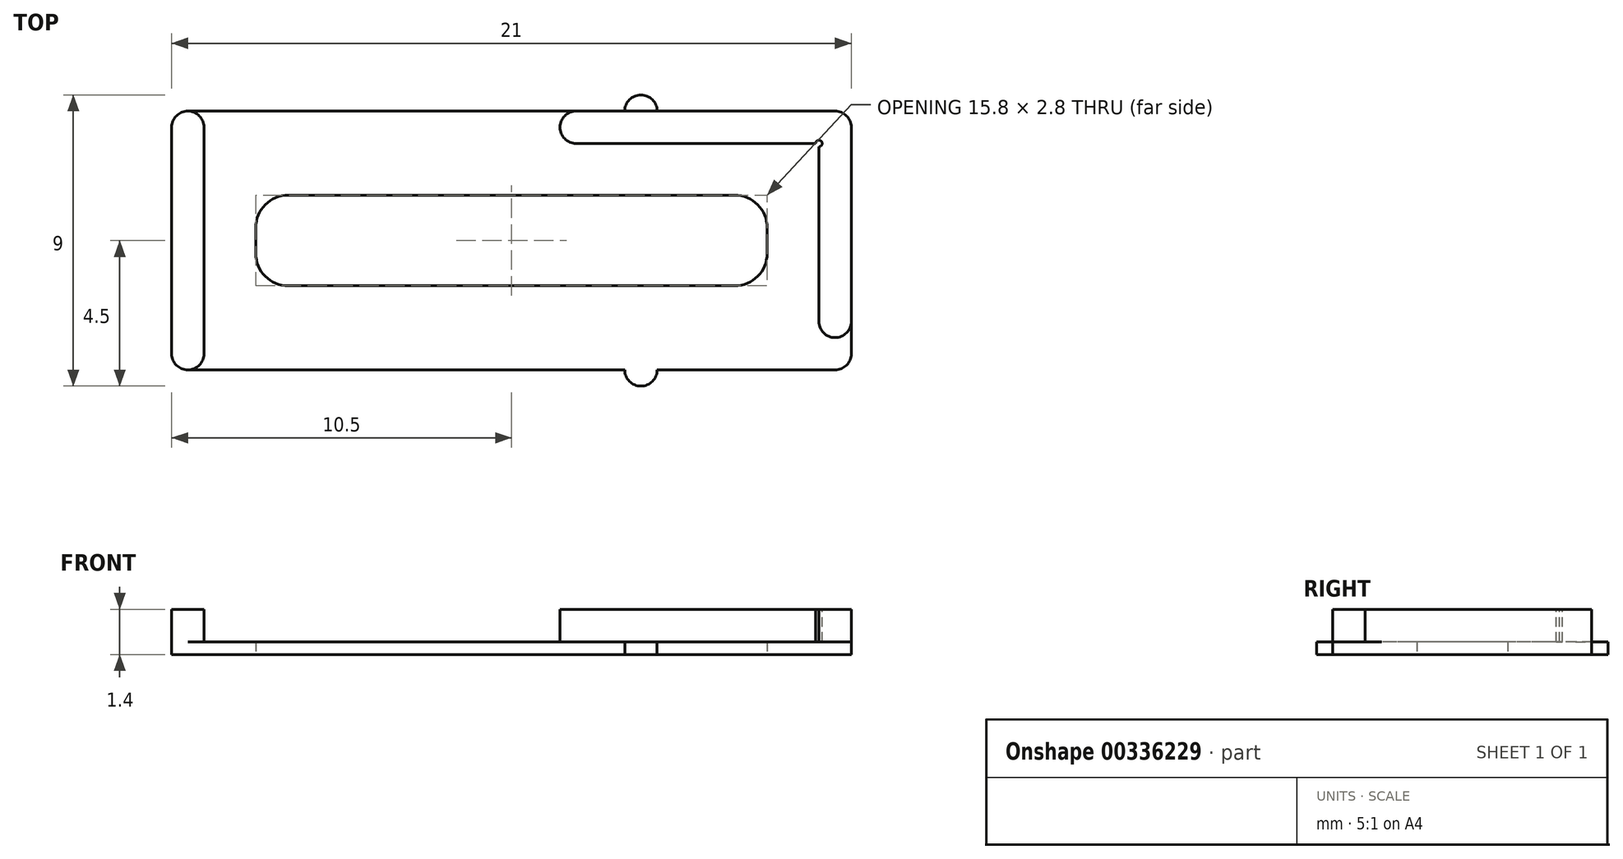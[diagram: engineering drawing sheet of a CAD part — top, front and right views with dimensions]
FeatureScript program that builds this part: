
annotation { "Feature Type Name" : "Feature", "Feature Type Description" : "" }
export const myFeature = defineFeature(function(context is Context, id is Id, definition is map)
    precondition{}
    {
        {
            var Q0;
            Q0=qCreatedBy(makeId("Top.planeOp"),FACE);
            var sketch = newSketch(context, id + "F0", { "sketchPlane" : qUnion([Q0])});
            skLineSegment(sketch, "E0.bottom", {"start": v(-4.5, 4.8) * mm, "end": v(4.5, 4.8) * mm});
            skLineSegment(sketch, "E0.top", {"start": v(-4.5, 0) * mm, "end": v(4.5, 0) * mm});
            skLineSegment(sketch, "E0.left", {"start": v(-4.5, 4.8) * mm, "end": v(-4.5, 0) * mm});
            skLineSegment(sketch, "E0.right", {"start": v(4.5, 4.8) * mm, "end": v(4.5, 0) * mm});
            skLineSegment(sketch, "E1", {"start": v(-4.5, 0) * mm, "end": v(-9.5, 0) * mm});
            skLineSegment(sketch, "E2", {"start": v(-9.5, 0) * mm, "end": v(-9.5, -6) * mm});
            skLineSegment(sketch, "E3", {"start": v(4.5, 0) * mm, "end": v(9.5, 0) * mm});
            skLineSegment(sketch, "E4", {"start": v(9.5, 0) * mm, "end": v(9.5, -6) * mm});
            skLineSegment(sketch, "E5", {"start": v(9.5, -6) * mm, "end": v(-9.5, -6) * mm});
            skLineSegment(sketch, "E6", {"start": v(-9.5, -1) * mm, "end": v(9.5, -1) * mm, "construction": true});
            skLineSegment(sketch, "E7", {"start": v(-9.5, -5.2) * mm, "end": v(9.5, -5.2) * mm, "construction": true});
            skPoint(sketch, "E8", {"position": v(4, -6) * mm});
            skPoint(sketch, "E9", {"position": v(4, 0) * mm});
            skSolve(sketch);
        }
        {
            var Q0;
            Q0=qCreatedBy(makeId("Front.planeOp"),FACE);
            var sketch = newSketch(context, id + "F1", { "sketchPlane" : qUnion([Q0])});
            skLineSegment(sketch, "E10", {"start": v(0, 0) * mm, "end": v(0, -0.4) * mm});
            skLineSegment(sketch, "E11", {"start": v(0, 0) * mm, "end": v(0, 1) * mm});
            skSolve(sketch);
        }
        {
            var Q0;
            Q0=qCreatedBy(makeId("Top.planeOp"),FACE);
            var sketch = newSketch(context, id + "F2", { "sketchPlane" : qUnion([Q0])});
            skLineSegment(sketch, "E12.0.0", {"start": v(4.5, 0) * mm, "end": v(-4.5, 0) * mm, "construction": true});
            skLineSegment(sketch, "E12.0.1", {"start": v(-4.5, 0) * mm, "end": v(-9.5, 0) * mm, "construction": true});
            skLineSegment(sketch, "E12.0.2", {"start": v(-9.5, 0) * mm, "end": v(-9.5, -6) * mm, "construction": true});
            skLineSegment(sketch, "E12.0.3", {"start": v(-9.5, -6) * mm, "end": v(9.5, -6) * mm, "construction": true});
            skLineSegment(sketch, "E12.0.4", {"start": v(9.5, -6) * mm, "end": v(9.5, 0) * mm, "construction": true});
            skLineSegment(sketch, "E12.0.5", {"start": v(9.5, 0) * mm, "end": v(4.5, 0) * mm, "construction": true});
            skLineSegment(sketch, "E13.bottom", {"start": v(10.5, 1) * mm, "end": v(-10.5, 1) * mm});
            skLineSegment(sketch, "E13.top", {"start": v(10.5, -7) * mm, "end": v(-10.5, -7) * mm});
            skLineSegment(sketch, "E13.left", {"start": v(10.5, 1) * mm, "end": v(10.5, -7) * mm});
            skLineSegment(sketch, "E13.right", {"start": v(-10.5, 1) * mm, "end": v(-10.5, -7) * mm});
            skLineSegment(sketch, "E14.0", {"start": v(-7.9, -1.6) * mm, "end": v(-7.9, -4.4) * mm});
            skLineSegment(sketch, "E14.1", {"start": v(7.9, -4.4) * mm, "end": v(7.9, -1.6) * mm});
            skLineSegment(sketch, "E14.2", {"start": v(7.9, -1.6) * mm, "end": v(4.5, -1.6) * mm});
            skLineSegment(sketch, "E14.3", {"start": v(-7.9, -4.4) * mm, "end": v(7.9, -4.4) * mm});
            skLineSegment(sketch, "E14.4", {"start": v(4.5, -1.6) * mm, "end": v(-4.5, -1.6) * mm});
            skLineSegment(sketch, "E14.5", {"start": v(-4.5, -1.6) * mm, "end": v(-7.9, -1.6) * mm});
            skArc(sketch, "E15", {"start": v(3.5, 1) * mm, "mid": v(4, 1.5) * mm, "end": v(4.5, 1) * mm});
            skArc(sketch, "E16", {"start": v(3.5, -7) * mm, "mid": v(4, -7.5) * mm, "end": v(4.5, -7) * mm});
            skSolve(sketch);
        }
        {
            var Q0;
            Q0 = qSketchRegion(id + "F2", true);
            var Q1;
            Q1=sQuery(id+"F1.wireOp",EDGE,"E10");
            sweep(context, id + "F3", {"profiles" : qUnion([Q0]), "path" : qUnion([Q1])});
        }
        {
            var Q0;
            Q0=makeQuery(id+"F2.imprint","IMPRINT",FACE,{"disambiguationData":[TD([[makeQuery(id+"F2.imprint","IMPRINT",EDGE,{"derivedFrom":sQuery(id+"F2.wireOp",EDGE,"E13.bottom")}),1.0]])]});
            var sketch = newSketch(context, id + "F4", { "sketchPlane" : qUnion([Q0])});
            skLineSegment(sketch, "E17.0", {"start": v(9.5, 0) * mm, "end": v(9.5, -6) * mm});
            skLineSegment(sketch, "E18.0", {"start": v(-9.5, 0) * mm, "end": v(-9.5, -6) * mm});
            skLineSegment(sketch, "E19.0", {"start": v(4.5, 0) * mm, "end": v(9.5, 0) * mm, "construction": true});
            skLineSegment(sketch, "E20.0", {"start": v(-4.5, 0) * mm, "end": v(-9.5, 0) * mm, "construction": true});
            skLineSegment(sketch, "E21.0.0", {"start": v(4.5, -7) * mm, "end": v(10.5, -7) * mm, "construction": true});
            skLineSegment(sketch, "E21.0.1", {"start": v(10.5, -7) * mm, "end": v(10.5, 1) * mm, "construction": true});
            skLineSegment(sketch, "E21.0.2", {"start": v(10.5, 1) * mm, "end": v(4.5, 1) * mm, "construction": true});
            skLineSegment(sketch, "E21.0.3", {"start": v(-10.5, 1) * mm, "end": v(-10.5, -7) * mm, "construction": true});
            skLineSegment(sketch, "E22", {"start": v(4.5, 1) * mm, "end": v(4.5, -7) * mm});
            skLineSegment(sketch, "E23", {"start": v(-9.5, 0) * mm, "end": v(-9.5, 1) * mm});
            skLineSegment(sketch, "E24", {"start": v(-9.5, 1) * mm, "end": v(-10.5, 1) * mm});
            skLineSegment(sketch, "E25", {"start": v(-9.5, -6) * mm, "end": v(-9.5, -7) * mm});
            skLineSegment(sketch, "E26", {"start": v(-9.5, -7) * mm, "end": v(-10.5, -7) * mm});
            skLineSegment(sketch, "E27", {"start": v(10.5, 1) * mm, "end": v(10.5, -6) * mm});
            skLineSegment(sketch, "E28", {"start": v(10.5, 1) * mm, "end": v(1.5, 1) * mm});
            skLineSegment(sketch, "E29", {"start": v(1.5, 1) * mm, "end": v(1.5, 0) * mm});
            skLineSegment(sketch, "E30", {"start": v(1.5, 0) * mm, "end": v(9.5, 0) * mm});
            skLineSegment(sketch, "E31", {"start": v(9.5, -6) * mm, "end": v(10.5, -6) * mm});
            skLineSegment(sketch, "E32", {"start": v(-10.5, 1) * mm, "end": v(-10.5, -7) * mm});
            skSolve(sketch);
        }
        {
            var Q0;
            Q0 = qSketchRegion(id + "F4", true);
            var Q1;
            Q1=sQuery(id+"F1.wireOp",EDGE,"E11");
            sweep(context, id + "F5", {"operationType" : NewBodyOperationType.ADD, "profiles" : qUnion([Q0]), "path" : qUnion([Q1])});
        }
        {
            var Q0;
            Q0=makeQuery(id+"F3.opSweep","SWEPT_EDGE",EDGE,{"disambiguationData":[OSD([sQuery(id+"F1.wireOp",EDGE,"E10"),sQuery(id+"F2.wireOp",EDGE,"E14.0"),sQuery(id+"F2.wireOp",EDGE,"E14.5")])]});
            var Q1;
            Q1=makeQuery(id+"F3.opSweep","SWEPT_EDGE",EDGE,{"disambiguationData":[OSD([sQuery(id+"F1.wireOp",EDGE,"E10"),sQuery(id+"F2.wireOp",EDGE,"E14.0"),sQuery(id+"F2.wireOp",EDGE,"E14.3")])]});
            var Q2;
            Q2=makeQuery(id+"F3.opSweep","SWEPT_EDGE",EDGE,{"disambiguationData":[OSD([sQuery(id+"F1.wireOp",EDGE,"E10"),sQuery(id+"F2.wireOp",EDGE,"E14.1"),sQuery(id+"F2.wireOp",EDGE,"E14.2")])]});
            var Q3;
            Q3=makeQuery(id+"F3.opSweep","SWEPT_EDGE",EDGE,{"disambiguationData":[OSD([sQuery(id+"F1.wireOp",EDGE,"E10"),sQuery(id+"F2.wireOp",EDGE,"E14.1"),sQuery(id+"F2.wireOp",EDGE,"E14.3")])]});
            fillet(context, id + "F6", {"entities" : qUnion([Q0, Q1, Q2, Q3]), "radius" : 1 * mm, "allowEdgeOverflow" : false});
        }
        {
            var Q0;
            Q0=makeQuery(id+"F5.boolean.opBoolean","MERGE",EDGE,{"derivedFrom":[makeQuery(id+"F3.opSweep","SWEPT_EDGE",EDGE,{"disambiguationData":[OSD([sQuery(id+"F1.wireOp",EDGE,"E10"),sQuery(id+"F2.wireOp",EDGE,"E13.top"),sQuery(id+"F2.wireOp",EDGE,"E13.right")])]}),makeQuery(id+"F5.opSweep","SWEPT_EDGE",EDGE,{"disambiguationData":[OSD([sQuery(id+"F1.wireOp",EDGE,"E11"),sQuery(id+"F4.wireOp",EDGE,"E22"),sQuery(id+"F4.wireOp",EDGE,"E26")])]})]});
            var Q1;
            Q1=makeQuery(id+"F5.boolean.opBoolean","MERGE",EDGE,{"derivedFrom":[makeQuery(id+"F3.opSweep","SWEPT_EDGE",EDGE,{"disambiguationData":[OSD([sQuery(id+"F1.wireOp",EDGE,"E10"),sQuery(id+"F2.wireOp",EDGE,"E13.bottom"),sQuery(id+"F2.wireOp",EDGE,"E13.right")])]}),makeQuery(id+"F5.opSweep","SWEPT_EDGE",EDGE,{"disambiguationData":[OSD([sQuery(id+"F1.wireOp",EDGE,"E11"),sQuery(id+"F4.wireOp",EDGE,"E22"),sQuery(id+"F4.wireOp",EDGE,"E24")])]})]});
            var Q2;
            Q2=makeQuery(id+"F5.opSweep","SWEPT_EDGE",EDGE,{"disambiguationData":[OSD([sQuery(id+"F1.wireOp",EDGE,"E11"),sQuery(id+"F2.wireOp",EDGE,"E13.bottom"),sQuery(id+"F4.wireOp",EDGE,"E23"),sQuery(id+"F4.wireOp",EDGE,"E24")])]});
            var Q3;
            Q3=makeQuery(id+"F5.opSweep","SWEPT_EDGE",EDGE,{"disambiguationData":[OSD([sQuery(id+"F1.wireOp",EDGE,"E11"),sQuery(id+"F2.wireOp",EDGE,"E13.top"),sQuery(id+"F4.wireOp",EDGE,"E25"),sQuery(id+"F4.wireOp",EDGE,"E26")])]});
            var Q4;
            Q4=makeQuery(id+"F5.opSweep","SWEPT_EDGE",EDGE,{"disambiguationData":[OSD([sQuery(id+"F1.wireOp",EDGE,"E11"),sQuery(id+"F4.wireOp",EDGE,"E17.0"),sQuery(id+"F4.wireOp",EDGE,"E31")])]});
            var Q5;
            Q5=makeQuery(id+"F5.opSweep","SWEPT_EDGE",EDGE,{"disambiguationData":[OSD([sQuery(id+"F1.wireOp",EDGE,"E11"),sQuery(id+"F4.wireOp",EDGE,"E27"),sQuery(id+"F4.wireOp",EDGE,"E31")])]});
            var Q6;
            Q6=makeQuery(id+"F5.opSweep","SWEPT_EDGE",EDGE,{"disambiguationData":[OSD([sQuery(id+"F1.wireOp",EDGE,"E11"),sQuery(id+"F2.wireOp",EDGE,"E13.bottom"),sQuery(id+"F4.wireOp",EDGE,"E27"),sQuery(id+"F4.wireOp",EDGE,"E28")])]});
            var Q7;
            Q7=makeQuery(id+"F5.opSweep","SWEPT_EDGE",EDGE,{"disambiguationData":[OSD([sQuery(id+"F1.wireOp",EDGE,"E11"),sQuery(id+"F2.wireOp",EDGE,"E13.bottom"),sQuery(id+"F4.wireOp",EDGE,"E28"),sQuery(id+"F4.wireOp",EDGE,"E29")])]});
            var Q8;
            Q8=makeQuery(id+"F5.opSweep","SWEPT_EDGE",EDGE,{"disambiguationData":[OSD([sQuery(id+"F1.wireOp",EDGE,"E11"),sQuery(id+"F4.wireOp",EDGE,"E29"),sQuery(id+"F4.wireOp",EDGE,"E30")])]});
            var Q9;
            Q9=makeQuery(id+"F3.opSweep","SWEPT_EDGE",EDGE,{"disambiguationData":[OSD([sQuery(id+"F1.wireOp",EDGE,"E10"),sQuery(id+"F2.wireOp",EDGE,"E13.top"),sQuery(id+"F2.wireOp",EDGE,"E13.left")])]});
            fillet(context, id + "F7", {"entities" : qUnion([Q0, Q1, Q2, Q3, Q4, Q5, Q6, Q7, Q8, Q9]), "radius" : 0.5 * mm, "allowEdgeOverflow" : false});
        }
        {
            var Q0;
            Q0=makeQuery(id+"F5.opSweep","CAP_FACE",FACE,{"disambiguationData":[OSD([sQuery(id+"F1.wireOp",VERTEX,"E11.end"),sQuery(id+"F4.wireOp",EDGE,"E17.0"),sQuery(id+"F4.wireOp",EDGE,"E27"),sQuery(id+"F4.wireOp",EDGE,"E28"),sQuery(id+"F4.wireOp",EDGE,"E29"),sQuery(id+"F4.wireOp",EDGE,"E30"),sQuery(id+"F4.wireOp",EDGE,"E31")])],"isStart":false});
            var sketch = newSketch(context, id + "F8", { "sketchPlane" : qUnion([Q0])});
            skCircle(sketch, "E33", {"center": v(9.5, 0) * mm, "radius": 0.1 * mm});
            skSolve(sketch);
        }
        {
            var Q0;
            Q0 = qSketchRegion(id + "F8", true);
            var Q1;
            Q1=makeQuery(id+"F3.opSweep","CAP_FACE",FACE,{"disambiguationData":[OSD([sQuery(id+"F1.wireOp",VERTEX,"E10.start"),sQuery(id+"F2.wireOp",EDGE,"E13.bottom"),sQuery(id+"F2.wireOp",EDGE,"E13.top"),sQuery(id+"F2.wireOp",EDGE,"E13.left"),sQuery(id+"F2.wireOp",EDGE,"E13.right"),sQuery(id+"F2.wireOp",EDGE,"E14.0"),sQuery(id+"F2.wireOp",EDGE,"E14.1"),sQuery(id+"F2.wireOp",EDGE,"E14.2"),sQuery(id+"F2.wireOp",EDGE,"E14.3"),sQuery(id+"F2.wireOp",EDGE,"E14.4"),sQuery(id+"F2.wireOp",EDGE,"E14.5")])],"isStart":true});
            extrude(context, id + "F9", {"entities" : qUnion([Q0]), "operationType" : NewBodyOperationType.REMOVE, "endBound" : BoundingType.UP_TO_SURFACE, "oppositeDirection" : true, "endBoundEntityFace" : qUnion([Q1]), "depth" : 25 * mm});
        }
    });
